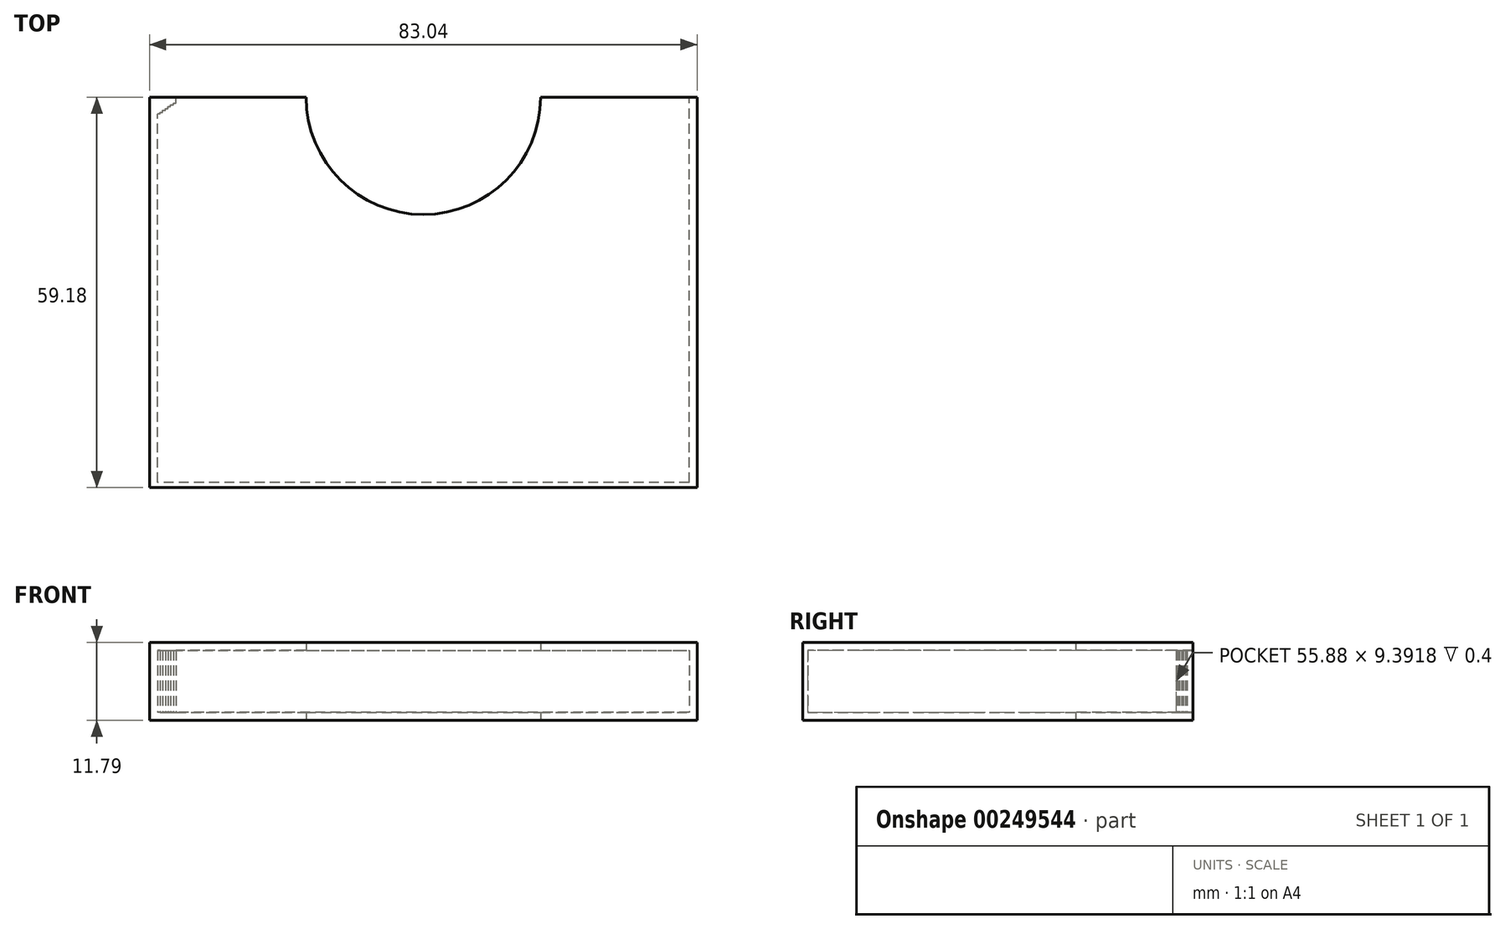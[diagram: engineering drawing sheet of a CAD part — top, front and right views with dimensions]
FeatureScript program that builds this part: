
annotation { "Feature Type Name" : "Feature", "Feature Type Description" : "" }
export const myFeature = defineFeature(function(context is Context, id is Id, definition is map)
    precondition{}
    {
        {
            var Q0;
            Q0=qCreatedBy(makeId("Top.planeOp"),FACE);
            var sketch = newSketch(context, id + "F0", { "sketchPlane" : qUnion([Q0])});
            skLineSegment(sketch, "E0.bottom", {"start": v(-40.32, 58.42) * mm, "end": v(40.32, 58.42) * mm});
            skLineSegment(sketch, "E0.top", {"start": v(-40.32, 0) * mm, "end": v(40.32, 0) * mm});
            skLineSegment(sketch, "E0.left", {"start": v(-40.32, 58.42) * mm, "end": v(-40.32, 0) * mm});
            skLineSegment(sketch, "E0.right", {"start": v(40.32, 58.42) * mm, "end": v(40.32, 0) * mm});
            skArc(sketch, "E1", {"start": v(-17.78, 58.42) * mm, "mid": v(0, 40.64) * mm, "end": v(17.78, 58.42) * mm});
            skLineSegment(sketch, "E2.0", {"start": v(41.52, 58.42) * mm, "end": v(41.52, -1.2) * mm});
            skLineSegment(sketch, "E2.1", {"start": v(-41.52, -1.2) * mm, "end": v(41.52, -1.2) * mm});
            skLineSegment(sketch, "E2.2", {"start": v(-41.52, 58.42) * mm, "end": v(-41.52, -1.2) * mm});
            skLineSegment(sketch, "E3", {"start": v(-40.32, 58.42) * mm, "end": v(-41.52, 58.42) * mm});
            skLineSegment(sketch, "E4", {"start": v(40.32, 58.42) * mm, "end": v(41.52, 58.42) * mm});
            skLineSegment(sketch, "E5", {"start": v(-41.52, -0.76) * mm, "end": v(-41.52, -1.2) * mm});
            skLineSegment(sketch, "E6", {"start": v(-41.52, -0.76) * mm, "end": v(41.52, -0.76) * mm});
            skLineSegment(sketch, "E7", {"start": v(41.52, -1.2) * mm, "end": v(41.52, -0.76) * mm});
            skSolve(sketch);
        }
        {
            var Q0;
            Q0=makeQuery(id+"F0.imprint","IMPRINT",FACE,{"disambiguationData":[TD([[makeQuery(id+"F0.imprint","IMPRINT",EDGE,{"derivedFrom":sQuery(id+"F0.wireOp",EDGE,"E0.top")}),1.0]])]});
            var Q1;
            Q1=makeQuery(id+"F0.imprint","IMPRINT",FACE,{"disambiguationData":[TD([[makeQuery(id+"F0.imprint","IMPRINT",EDGE,{"derivedFrom":sQuery(id+"F0.wireOp",EDGE,"E0.top")}),-1.0]])]});
            extrude(context, id + "F1", {"entities" : qUnion([Q0, Q1]), "depth" : .4 * mm * 3});
        }
        {
            var Q0;
            Q0=makeQuery(id+"F0.imprint","IMPRINT",FACE,{"disambiguationData":[TD([[makeQuery(id+"F0.imprint","IMPRINT",EDGE,{"derivedFrom":sQuery(id+"F0.wireOp",EDGE,"E0.top")}),-1.0]])]});
            extrude(context, id + "F2", {"entities" : qUnion([Q0]), "operationType" : NewBodyOperationType.ADD, "depth" : 10.6 * mm});
        }
        {
            var Q0;
            Q0=makeQuery(id+"F2.opExtrude","CAP_FACE",FACE,{"disambiguationData":[OSD([sQuery(id+"F0.wireOp",EDGE,"E0.top"),sQuery(id+"F0.wireOp",EDGE,"E0.left"),sQuery(id+"F0.wireOp",EDGE,"E0.right"),sQuery(id+"F0.wireOp",EDGE,"E2.0"),sQuery(id+"F0.wireOp",EDGE,"E2.2"),sQuery(id+"F0.wireOp",EDGE,"E3"),sQuery(id+"F0.wireOp",EDGE,"E4"),sQuery(id+"F0.wireOp",EDGE,"E6")])],"isStart":false});
            var sketch = newSketch(context, id + "F3", { "sketchPlane" : qUnion([Q0])});
            skLineSegment(sketch, "E8.0", {"start": v(-41.52, 58.42) * mm, "end": v(-41.52, -0.76) * mm});
            skLineSegment(sketch, "E9.0", {"start": v(-40.32, 58.42) * mm, "end": v(-17.78, 58.42) * mm});
            skArc(sketch, "E10.0", {"start": v(-17.78, 58.42) * mm, "mid": v(0, 40.64) * mm, "end": v(17.78, 58.42) * mm});
            skLineSegment(sketch, "E11.0", {"start": v(17.78, 58.42) * mm, "end": v(40.32, 58.42) * mm});
            skLineSegment(sketch, "E12.0", {"start": v(41.52, 58.42) * mm, "end": v(41.52, -0.76) * mm});
            skLineSegment(sketch, "E13.0", {"start": v(-41.52, -0.76) * mm, "end": v(41.52, -0.76) * mm});
            skLineSegment(sketch, "E14.0", {"start": v(40.32, 58.42) * mm, "end": v(41.52, 58.42) * mm});
            skLineSegment(sketch, "E15.0", {"start": v(-40.32, 58.42) * mm, "end": v(-41.52, 58.42) * mm});
            skSolve(sketch);
        }
        {
            var Q0;
            Q0 = qSketchRegion(id + "F3", true);
            extrude(context, id + "F4", {"entities" : qUnion([Q0]), "operationType" : NewBodyOperationType.ADD, "depth" : .4 * mm * 3});
        }
        {
            var Q0;
            Q0=makeQuery(id+"F1.opExtrude","CAP_FACE",FACE,{"disambiguationData":[OSD([sQuery(id+"F0.wireOp",EDGE,"E0.bottom"),sQuery(id+"F0.wireOp",EDGE,"E1"),sQuery(id+"F0.wireOp",EDGE,"E2.0"),sQuery(id+"F0.wireOp",EDGE,"E2.2"),sQuery(id+"F0.wireOp",EDGE,"E3"),sQuery(id+"F0.wireOp",EDGE,"E4"),sQuery(id+"F0.wireOp",EDGE,"E6")])],"isStart":false});
            var sketch = newSketch(context, id + "F5", { "sketchPlane" : qUnion([Q0])});
            skLineSegment(sketch, "E16", {"start": v(-39.92, 55.88) * mm, "end": v(-40.32, 55.88) * mm});
            skLineSegment(sketch, "E17", {"start": v(-40.32, 55.88) * mm, "end": v(-40.32, 58.42) * mm});
            skLineSegment(sketch, "E18", {"start": v(-39.92, 55.88) * mm, "end": v(-39.92, 56.16) * mm});
            skLineSegment(sketch, "E19", {"start": v(-39.92, 56.16) * mm, "end": v(-39.52, 56.16) * mm});
            skLineSegment(sketch, "E20", {"start": v(-39.52, 56.16) * mm, "end": v(-39.52, 56.44) * mm});
            skLineSegment(sketch, "E21", {"start": v(-39.52, 56.44) * mm, "end": v(-39.12, 56.44) * mm});
            skLineSegment(sketch, "E22", {"start": v(-39.12, 56.44) * mm, "end": v(-39.12, 56.72) * mm});
            skLineSegment(sketch, "E23", {"start": v(-39.12, 56.72) * mm, "end": v(-38.72, 56.72) * mm});
            skLineSegment(sketch, "E24", {"start": v(-38.72, 56.72) * mm, "end": v(-38.72, 57) * mm});
            skLineSegment(sketch, "E25", {"start": v(-38.72, 57) * mm, "end": v(-38.32, 57) * mm});
            skLineSegment(sketch, "E26", {"start": v(-38.32, 57) * mm, "end": v(-38.32, 57.28) * mm});
            skLineSegment(sketch, "E27", {"start": v(-38.32, 57.28) * mm, "end": v(-37.92, 57.28) * mm});
            skLineSegment(sketch, "E28", {"start": v(-37.92, 57.28) * mm, "end": v(-37.92, 57.56) * mm});
            skLineSegment(sketch, "E29", {"start": v(-37.92, 57.56) * mm, "end": v(-37.52, 57.56) * mm});
            skLineSegment(sketch, "E30", {"start": v(-37.52, 57.56) * mm, "end": v(-37.52, 58.42) * mm});
            skSolve(sketch);
        }
        {
            var Q0;
            Q0 = qSketchRegion(id + "F5", true);
            var Q1;
            Q1=makeQuery(id+"F5.imprint","IMPRINT",FACE,{"disambiguationData":[TD([[makeQuery(id+"F5.imprint","IMPRINT",EDGE,{"derivedFrom":sQuery(id+"F5.wireOp",EDGE,"E16")}),-1.0]])]});
            extrude(context, id + "F6", {"entities" : qUnion([Q0, Q1]), "operationType" : NewBodyOperationType.ADD, "endBound" : BoundingType.UP_TO_NEXT, "depth" : 25.4 * mm});
        }
    });
